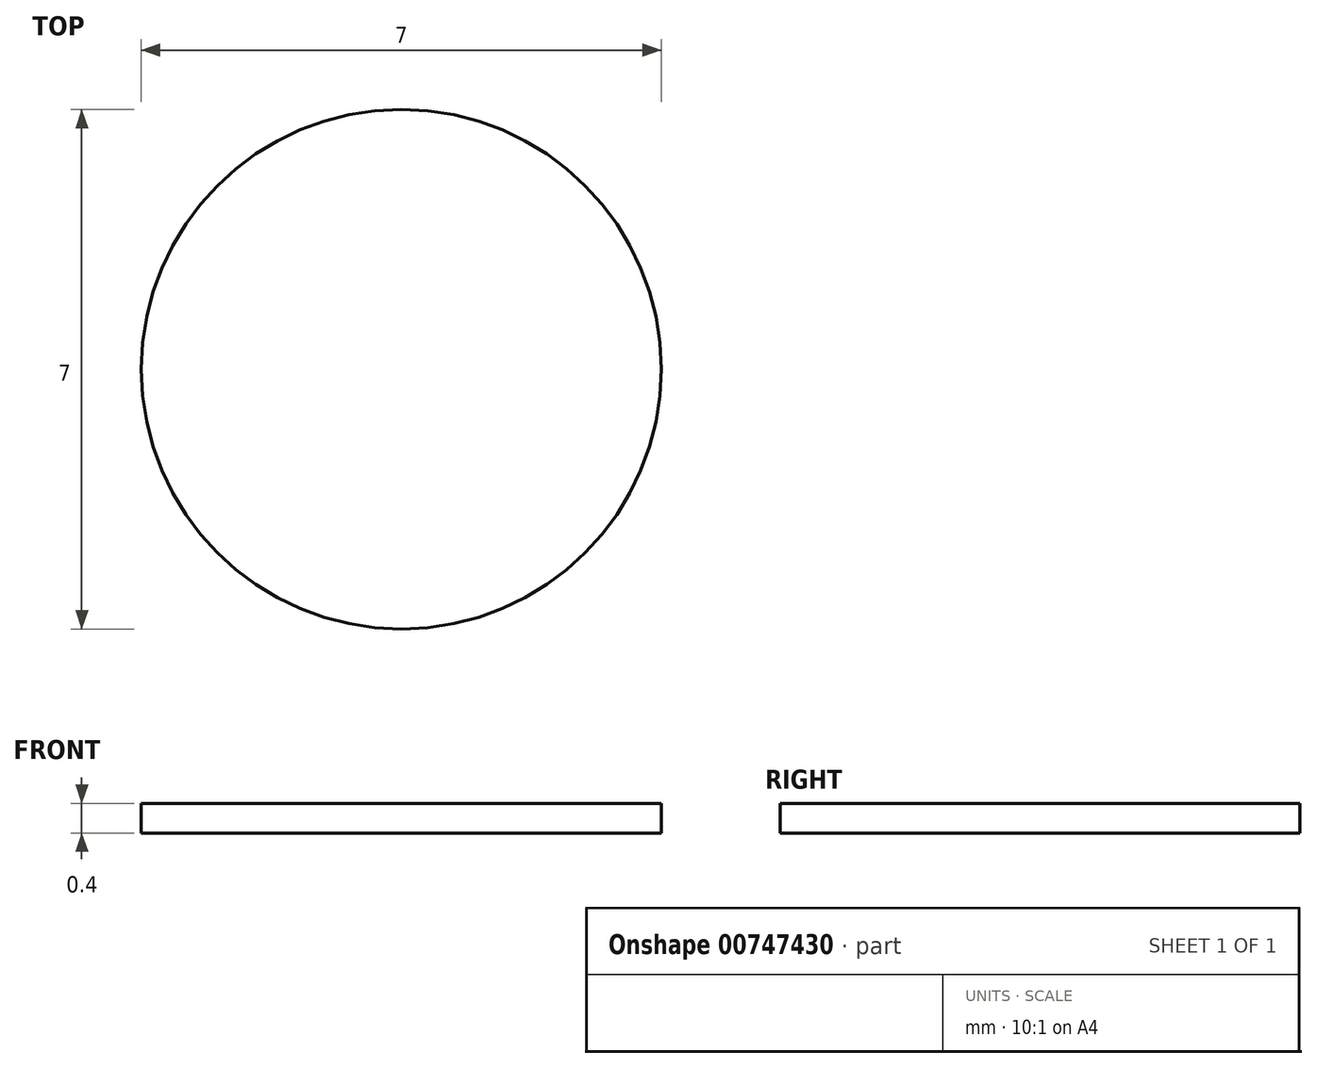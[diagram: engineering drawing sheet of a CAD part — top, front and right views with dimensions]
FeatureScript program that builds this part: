
annotation { "Feature Type Name" : "Feature", "Feature Type Description" : "" }
export const myFeature = defineFeature(function(context is Context, id is Id, definition is map)
    precondition{}
    {
        {
            var Q0;
            Q0=qCreatedBy(makeId("Top.planeOp"),FACE);
            var sketch = newSketch(context, id + "F0", { "sketchPlane" : qUnion([Q0])});
            skCircle(sketch, "E0", {"center": v(0, 0) * mm, "radius": 3.5 * mm});
            skCircle(sketch, "E1", {"center": v(0, 0) * mm, "radius": 3.7 * mm});
            skSolve(sketch);
        }
        {
            var Q0;
            Q0=makeQuery(id+"F0.imprint","IMPRINT",FACE,{"disambiguationData":[TD([[makeQuery(id+"F0.imprint","IMPRINT",EDGE,{"derivedFrom":sQuery(id+"F0.wireOp",EDGE,"E0")}),1.0]])]});
            extrude(context, id + "F1", {"entities" : qUnion([Q0]), "depth" : 0.4 * mm, "offsetDistance" : 25.4 * mm});
        }
    });
